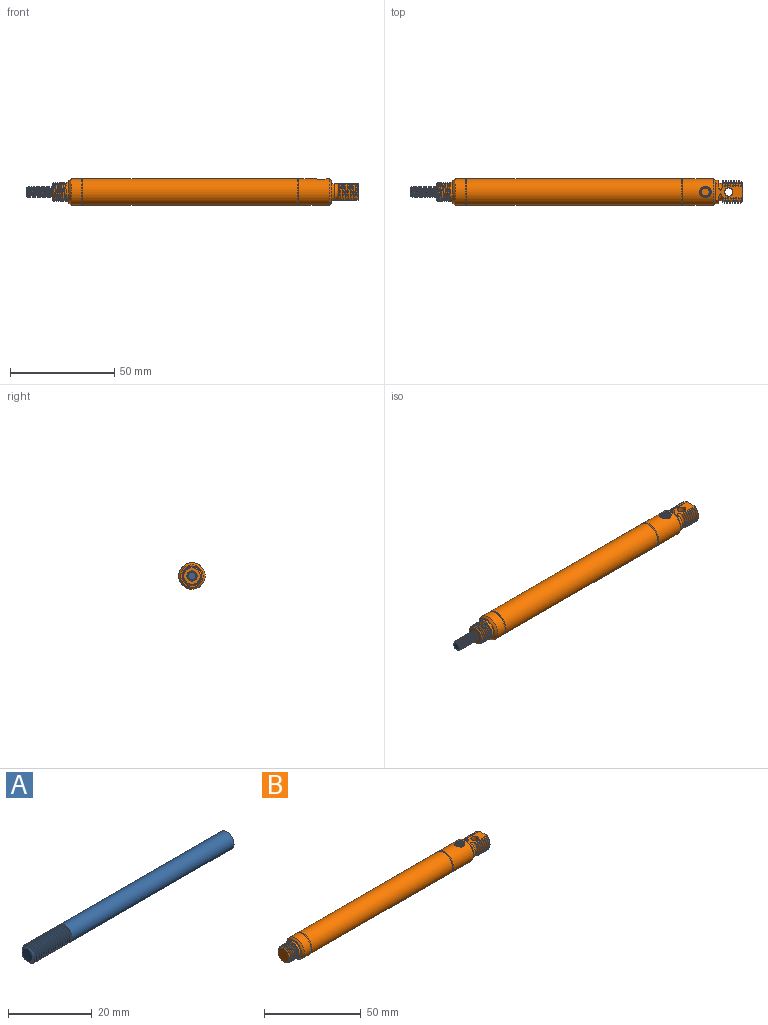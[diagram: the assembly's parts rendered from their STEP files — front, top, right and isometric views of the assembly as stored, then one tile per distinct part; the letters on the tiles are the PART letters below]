
ASSEMBLY  parts=2 mates=1
PART A: 23 faces, bbox 68x5.1x5.1 mm
  f0: cone r=1.82mm half-angle=45deg, axis (1,0,0), area 6.1mm2, adj f1,f17,f18,f19,f20
  f1: cylinder r=2.41mm len=4.83mm, axis (-1,0,0), area 1.2mm2, adj f0,f2,f18,f20
  f2: cylinder r=2.41mm len=4.83mm, axis (-1,0,0), area 1.5mm2, adj f1,f3,f18,f20
  f3: cylinder r=2.41mm len=4.83mm, axis (-1,0,0), area 1.5mm2, adj f2,f4,f18,f20
  f4: cylinder r=2.41mm len=4.83mm, axis (-1,0,0), area 1.5mm2, adj f3,f5,f18,f20
  f5: cylinder r=2.41mm len=4.83mm, axis (-1,0,0), area 1.5mm2, adj f4,f6,f18,f20
  f6: cylinder r=2.41mm len=4.83mm, axis (-1,0,0), area 1.5mm2, adj f5,f7,f18,f20
  f7: cylinder r=2.41mm len=4.83mm, axis (-1,0,0), area 1.5mm2, adj f6,f8,f18,f20
  f8: cylinder r=2.41mm len=4.83mm, axis (-1,0,0), area 1.5mm2, adj f7,f9,f18,f20
  f9: cylinder r=2.41mm len=4.83mm, axis (-1,0,0), area 1.5mm2, adj f8,f10,f18,f20
  f10: cylinder r=2.41mm len=4.83mm, axis (-1,0,0), area 1.5mm2, adj f9,f11,f18,f20
  f11: cylinder r=2.41mm len=4.83mm, axis (-1,0,0), area 1.5mm2, adj f10,f12,f18,f20
  f12: cylinder r=2.41mm len=4.83mm, axis (-1,0,0), area 1.5mm2, adj f11,f13,f18,f20
  f13: cylinder r=2.41mm len=4.83mm, axis (-1,0,0), area 1.5mm2, adj f12,f14,f18,f20
  f14: cylinder r=2.41mm len=4.83mm, axis (-1,0,0), area 1.5mm2, adj f13,f15,f18,f20
  f15: cylinder r=2.41mm len=4.83mm, axis (-1,0,0), area 1.5mm2, adj f14,f16,f18,f20
  f16: cylinder r=2.41mm len=55.13mm, axis (-1,0,0), area 830.5mm2, adj f15,f18,f20,f21,f22
  f17: plane 3.64x3.64mm, normal (-1,0,0), area 10.4mm2, adj f0
  f18: bspline ~13.1x4.83mm, area 125.6mm2, adj f0,f1,f2,f3,f4,f5,f6,f7
  f19: cylinder r=1.9mm len=12.62mm, axis (-1,0,0), area 18.8mm2, adj f0,f18,f20,f21
  f20: bspline ~13.22x4.52mm, area 125.7mm2, adj f0,f1,f2,f3,f4,f5,f6,f7
  f21: plane 5.13x5.13mm, normal (-1,0,0), area 3.6mm2, adj f16,f18,f19,f20
  f22: plane 4.83x4.83mm, normal (1,0,0), area 18.3mm2, adj f16
PART B: 116 faces, bbox 147.5x13.4x13.1 mm
  f0: torus R=5.18mm, axis (-1,0,0), area 35mm2, adj f42,f47,f96,f98,f99
  f1: torus R=5.18mm, axis (-1,0,0), area 29.9mm2, adj f25,f39,f43,f64,f65,f98,f99
  f2: cone r=4.76mm half-angle=45deg, axis (1,0,0), area 23.9mm2, adj f9,f111,f112,f113,f114
  f3: cylinder r=4.76mm len=9.53mm, axis (1,0,0), area 39.7mm2, adj f4,f103,f111,f113,f115
  f4: cylinder r=4.76mm len=9.53mm, axis (1,0,0), area 4mm2, adj f3,f5,f111,f113
  f5: cylinder r=4.76mm len=9.53mm, axis (1,0,0), area 4mm2, adj f4,f6,f111,f113
  f6: cylinder r=4.76mm len=9.53mm, axis (1,0,0), area 4mm2, adj f5,f7,f111,f113
  f7: cylinder r=4.76mm len=9.53mm, axis (1,0,0), area 4mm2, adj f6,f8,f111,f113
  f8: cylinder r=4.76mm len=9.53mm, axis (1,0,0), area 4mm2, adj f7,f9,f111,f113
  f9: cylinder r=4.76mm len=3.37mm, axis (1,0,0), area 0.2mm2, adj f2,f8,f113
  f10: cylinder r=2.41mm len=4.83mm, axis (0,0,1), area 9.1mm2, adj f106,f107,f109,f110
  f11: cone r=2.65mm half-angle=15deg, axis (0,0,1), area 2.6mm2, adj f20,f106
  f12: cone r=6.35mm half-angle=45deg, axis (-1,0,0), area 52.7mm2, adj f20,f23,f24,f100,f101
  f13: cone r=5.33mm half-angle=45deg, axis (1,0,0), area 52.7mm2, adj f16,f103
  f14: cone r=6.03mm half-angle=45deg, axis (1,0,0), area 17.5mm2, adj f20,f104
  f15: cone r=6.35mm half-angle=26.6deg, axis (-1,0,0), area 14mm2, adj f19,f104
  f16: cylinder r=6.35mm len=12.7mm, axis (-1,0,0), area 200.1mm2, adj f13,f17
  f17: cone r=6.35mm half-angle=45deg, axis (-1,0,0), area 17.5mm2, adj f16,f102
  f18: cone r=6.19mm half-angle=26.6deg, axis (1,0,0), area 14mm2, adj f19,f102
  f19: cylinder r=6.35mm len=102.74mm, axis (-1,0,0), area 4099.3mm2, adj f15,f18
  f20: cylinder r=6.35mm len=14.67mm, axis (-1,0,0), area 565.7mm2, adj f11,f12,f14,f105
  f21: cone r=2.41mm half-angle=45deg, axis (0,0,1), area 5.1mm2, adj f106,f107,f108,f109
  f22: cylinder r=1.98mm len=7.87mm, axis (0,0,1), area 98mm2, adj f98,f99
  f23: plane 7.87x1.96mm, normal (-1,0,0), area 2mm2, adj f12,f97,f98,f99
  f24: plane 7.87x1.96mm, normal (-1,0,0), area 2mm2, adj f12,f44,f98,f99
  f25: bspline ~9.6x3.48mm, area 2.3mm2, adj f1,f39,f43,f99
  f26: cylinder r=5.56mm len=7.87mm, axis (1,0,0), area 1.4mm2, adj f34,f37,f98,f99
  f27: cylinder r=5.56mm len=7.87mm, axis (1,0,0), area 1.4mm2, adj f33,f36,f98,f99
  f28: cylinder r=5.56mm len=7.87mm, axis (1,0,0), area 1.4mm2, adj f32,f35,f98,f99
  f29: cylinder r=4.73mm len=7.87mm, axis (-1,0,0), area 1.5mm2, adj f35,f41,f98,f99
  f30: cylinder r=4.73mm len=7.87mm, axis (-1,0,0), area 1.5mm2, adj f32,f36,f98,f99
  f31: cylinder r=4.73mm len=7.87mm, axis (-1,0,0), area 1.5mm2, adj f33,f37,f98,f99
  f32: bspline ~10.34x3.83mm, area 8.6mm2, adj f28,f30,f98,f99
  f33: bspline ~10.34x3.83mm, area 8.6mm2, adj f27,f31,f98,f99
  f34: bspline ~10.34x3.83mm, area 8.6mm2, adj f26,f79,f98,f99
  f35: bspline ~10.34x3.83mm, area 8.7mm2, adj f28,f29,f98,f99
  f36: bspline ~10.34x3.83mm, area 8.7mm2, adj f27,f30,f98,f99
  f37: bspline ~10.34x3.83mm, area 8.7mm2, adj f26,f31,f98,f99
  f38: bspline ~10.34x3.83mm, area 8.6mm2, adj f39,f67,f98,f99
  f39: cylinder r=4.73mm len=7.87mm, axis (-1,0,0), area 1.5mm2, adj f1,f25,f38,f98,f99
  f40: cone r=4.76mm half-angle=45deg, axis (-1,0,0), area 5mm2, adj f77,f81,f98,f99
  f41: bspline ~9.25x2.93mm, area 8.4mm2, adj f29,f76,f78,f98,f99
  f42: plane 7.87x2.2mm, normal (1,0,0), area 3.4mm2, adj f0,f97,f98,f99
  f43: plane 0.26x0.24mm, normal (-1,0,0), area 0mm2, adj f1,f25,f99
  f44: cylinder r=5.56mm len=7.87mm, axis (1,0,0), area 11.1mm2, adj f24,f95,f98,f99
  f45: cylinder r=5.56mm len=7.87mm, axis (1,0,0), area 1.3mm2, adj f46,f47,f96,f98,f99
  f46: bspline ~10.34x3.83mm, area 8.7mm2, adj f45,f70,f98,f99
  f47: bspline ~6.82x2.36mm, area 1.9mm2, adj f0,f45,f96,f98
  f48: cylinder r=5.56mm len=7.87mm, axis (1,0,0), area 1.4mm2, adj f58,f62,f98,f99
  f49: cylinder r=5.56mm len=7.87mm, axis (1,0,0), area 1.4mm2, adj f57,f61,f98,f99
  f50: cylinder r=5.56mm len=7.87mm, axis (1,0,0), area 1.4mm2, adj f56,f60,f98,f99
  f51: cone r=4.76mm half-angle=45deg, axis (-1,0,0), area 0.3mm2, adj f59,f77,f98
  f52: cylinder r=4.73mm len=7.87mm, axis (-1,0,0), area 1.5mm2, adj f60,f81,f98,f99
  f53: cylinder r=4.73mm len=7.87mm, axis (-1,0,0), area 1.5mm2, adj f56,f61,f98,f99
  f54: cylinder r=4.73mm len=7.87mm, axis (-1,0,0), area 1.5mm2, adj f57,f62,f98,f99
  f55: cylinder r=4.73mm len=7.87mm, axis (-1,0,0), area 1.5mm2, adj f58,f63,f98,f99
  f56: bspline ~10.34x3.83mm, area 8.6mm2, adj f50,f53,f98,f99
  f57: bspline ~10.34x3.83mm, area 8.6mm2, adj f49,f54,f98,f99
  f58: bspline ~10.34x3.83mm, area 8.6mm2, adj f48,f55,f98,f99
  f59: bspline ~4.84x2.7mm, area 0.4mm2, adj f51,f77,f80,f98
  f60: bspline ~10.34x3.83mm, area 8.7mm2, adj f50,f52,f98,f99
  f61: bspline ~10.34x3.83mm, area 8.7mm2, adj f49,f53,f98,f99
  f62: bspline ~10.34x3.83mm, area 8.7mm2, adj f48,f54,f98,f99
  f63: bspline ~10.34x3.83mm, area 8.7mm2, adj f55,f71,f98,f99
  f64: cylinder r=4.73mm len=3.94mm, axis (-1,0,0), area 0.3mm2, adj f1,f65,f66,f95,f99
  f65: bspline ~7.21x2.69mm, area 0.4mm2, adj f1,f64,f95,f98
  f66: cylinder r=9.69mm len=0.74mm, axis (-0.5,-0.58,-0.65), area 0mm2, adj f64,f95,f99
  f67: cylinder r=5.56mm len=7.87mm, axis (1,0,0), area 1.4mm2, adj f38,f68,f98,f99
  f68: bspline ~10.34x3.83mm, area 8.7mm2, adj f67,f94,f98,f99
  f69: bspline ~10.34x3.83mm, area 8.6mm2, adj f70,f75,f98,f99
  f70: cylinder r=4.73mm len=7.87mm, axis (-1,0,0), area 1.5mm2, adj f46,f69,f98,f99
  f71: cylinder r=5.56mm len=7.87mm, axis (1,0,0), area 1.4mm2, adj f63,f85,f98,f99
  f72: cylinder r=5.56mm len=7.87mm, axis (1,0,0), area 1.4mm2, adj f83,f88,f98,f99
  f73: cylinder r=5.56mm len=7.87mm, axis (1,0,0), area 1.4mm2, adj f86,f91,f98,f99
  f74: cylinder r=5.56mm len=7.87mm, axis (1,0,0), area 1.4mm2, adj f89,f93,f98,f99
  f75: cylinder r=5.56mm len=7.87mm, axis (1,0,0), area 1.4mm2, adj f69,f92,f98,f99
  f76: cylinder r=5.56mm len=3.94mm, axis (1,0,0), area 0.3mm2, adj f41,f78,f82,f98
  f77: plane 9.51x7.88mm, normal (1,0,0), area 65.1mm2, adj f40,f51,f59,f78,f80,f82,f98,f99
  f78: cone r=4.76mm half-angle=45deg, axis (-1,0,0), area 4.6mm2, adj f41,f76,f77,f82,f99
  f79: cylinder r=4.73mm len=7.87mm, axis (-1,0,0), area 1.5mm2, adj f34,f83,f98,f99
  f80: cylinder r=4.73mm len=7.28mm, axis (-1,0,0), area 1mm2, adj f59,f77,f82,f98
  f81: bspline ~9.9x3.59mm, area 4.5mm2, adj f40,f52,f98,f99
  f82: bspline ~8.9x2.93mm, area 4.5mm2, adj f76,f77,f78,f80,f98
  f83: bspline ~10.34x3.83mm, area 8.7mm2, adj f72,f79,f98,f99
  f84: cylinder r=4.73mm len=7.87mm, axis (-1,0,0), area 1.5mm2, adj f85,f86,f98,f99
  f85: bspline ~10.34x3.83mm, area 8.6mm2, adj f71,f84,f98,f99
  f86: bspline ~10.34x3.83mm, area 8.7mm2, adj f73,f84,f98,f99
  f87: cylinder r=4.73mm len=7.87mm, axis (-1,0,0), area 1.5mm2, adj f88,f89,f98,f99
  f88: bspline ~10.34x3.83mm, area 8.6mm2, adj f72,f87,f98,f99
  f89: bspline ~10.34x3.83mm, area 8.7mm2, adj f74,f87,f98,f99
  f90: cylinder r=4.73mm len=7.87mm, axis (-1,0,0), area 1.5mm2, adj f91,f92,f98,f99
  f91: bspline ~10.34x3.83mm, area 8.6mm2, adj f73,f90,f98,f99
  f92: bspline ~10.34x3.83mm, area 8.7mm2, adj f75,f90,f98,f99
  f93: bspline ~10.34x3.83mm, area 8.6mm2, adj f74,f94,f98,f99
  f94: cylinder r=4.73mm len=7.87mm, axis (-1,0,0), area 1.5mm2, adj f68,f93,f98,f99
  f95: plane 7.91x2.86mm, normal (1,0,0), area 6.6mm2, adj f44,f64,f65,f66,f98,f99
  f96: plane 7.02x2.16mm, normal (-1,0,0), area 1.8mm2, adj f0,f45,f47,f99
  f97: cylinder r=5.56mm len=7.87mm, axis (1,0,0), area 11.1mm2, adj f23,f42,f98,f99
  f98: plane 12.95x8.09mm, normal (0,0,1), area 64.8mm2, adj f0,f1,f22,f23,f24,f26,f27,f28
  f99: plane 12.95x8.09mm, normal (0,0,-1), area 64.5mm2, adj f0,f1,f22,f23,f24,f25,f26,f27
  f100: plane 7.2x1.4mm, normal (1,0,0), area 6.9mm2, adj f12,f99
  f101: plane 7.2x1.4mm, normal (1,0,0), area 6.9mm2, adj f12,f98
  f102: plane 12.38x12.38mm, normal (-1,0,0), area 6.1mm2, adj f17,f18
  f103: plane 10.67x10.67mm, normal (-1,0,0), area 18.1mm2, adj f3,f13
  f104: plane 12.38x12.38mm, normal (1,0,0), area 6.1mm2, adj f14,f15
  f105: cone r=2.65mm half-angle=15deg, axis (0,0,1), area 0mm2, adj f20,f106
  f106: plane 5.31x5.31mm, normal (0,0,1), area 3.8mm2, adj f10,f11,f21,f105
  f107: bspline ~5.56x4.83mm, area 45.1mm2, adj f10,f21,f108,f110
  f108: cylinder r=1.9mm len=4.31mm, axis (0,0,-1), area 6.5mm2, adj f21,f107,f109,f110
  f109: bspline ~5.12x4.83mm, area 46.7mm2, adj f10,f21,f108,f110
  f110: plane 4.67x4.63mm, normal (0,0,1), area 14.7mm2, adj f10,f107,f108,f109
  f111: bspline ~9.5x9.5mm, area 128mm2, adj f2,f3,f4,f5,f6,f7,f8,f112
  f112: cylinder r=4.08mm len=8.15mm, axis (1,0,0), area 20.9mm2, adj f2,f111,f113,f115
  f113: bspline ~9.52x9.52mm, area 139.6mm2, adj f2,f3,f4,f5,f6,f7,f8,f9
  f114: plane 7.94x7.94mm, normal (-1,0,0), area 49.5mm2, adj f2
  f115: plane 9.95x9.95mm, normal (-1,0,0), area 9.7mm2, adj f3,f111,f112,f113
PLACE A t=(-50.09,18.72,101.19)mm
PLACE B rot(axis=(1,0,0),0deg) t=(-50.09,18.72,101.19)mm
MATE slider A.f19 <-> B.f29  axis (-1,0,0) through (-129.59,18.72,101.19)mm
